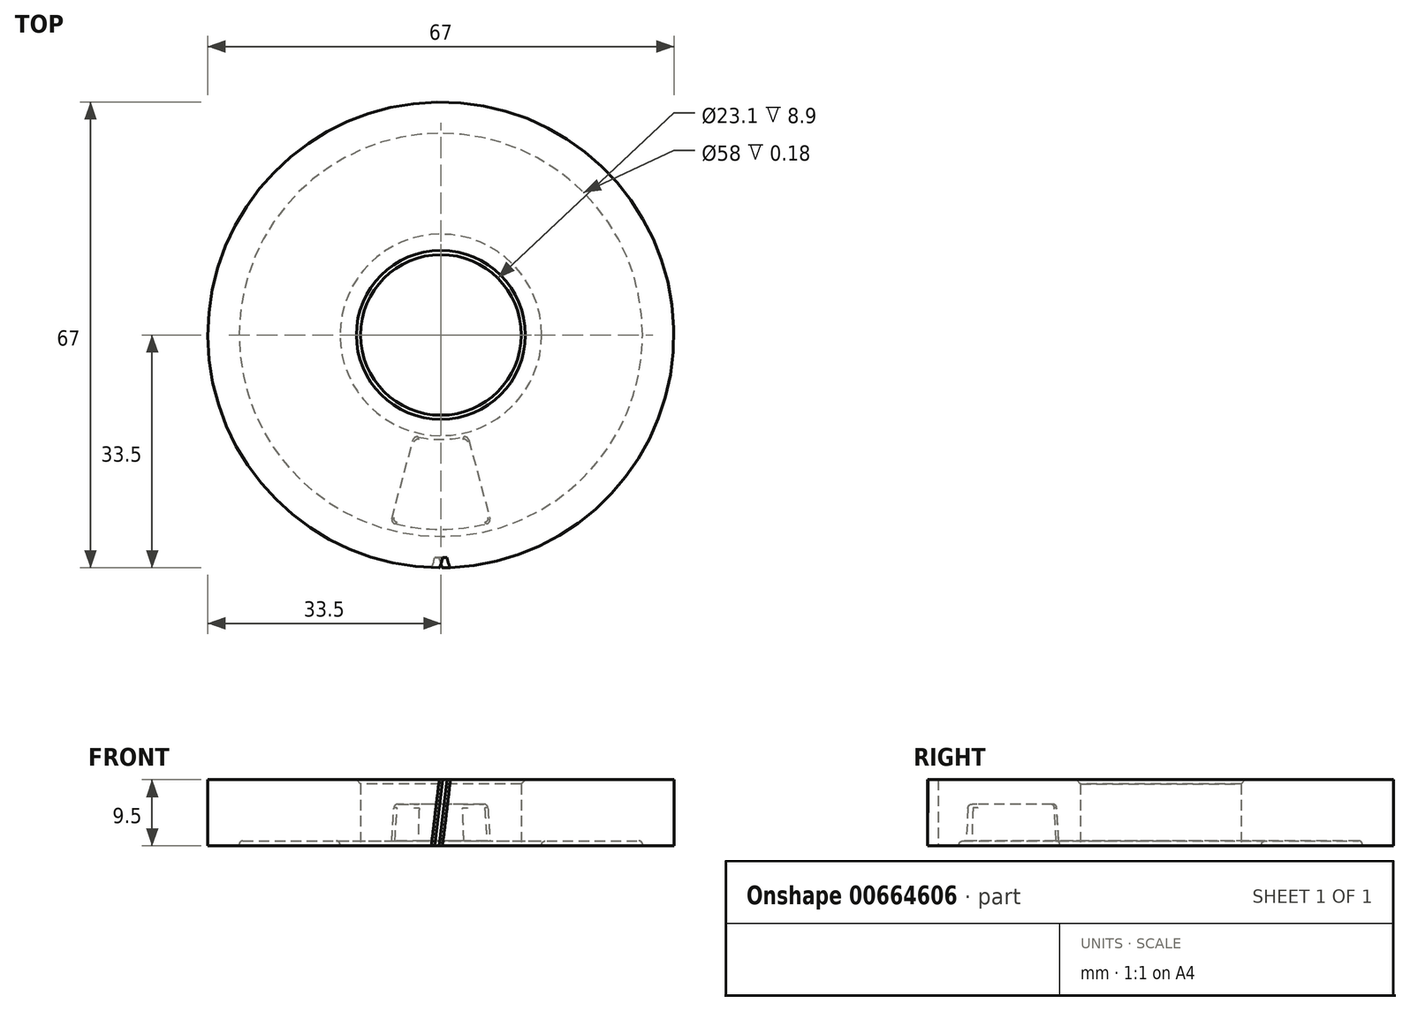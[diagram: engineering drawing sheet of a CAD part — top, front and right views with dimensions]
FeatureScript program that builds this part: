
annotation { "Feature Type Name" : "Feature", "Feature Type Description" : "" }
export const myFeature = defineFeature(function(context is Context, id is Id, definition is map)
    precondition{}
    {
        {
            var Q0;
            Q0=qCreatedBy(makeId("Top.planeOp"),FACE);
            var sketch = newSketch(context, id + "F0", { "sketchPlane" : qUnion([Q0])});
            skCircle(sketch, "E0", {"center": v(0, 0) * mm, "radius": 33.5 * mm});
            skCircle(sketch, "E1", {"center": v(0, 0) * mm, "radius": 11.55 * mm});
            skLineSegment(sketch, "E2", {"start": v(0, 55.87) * mm, "end": v(0, -59.32) * mm, "construction": true});
            skPoint(sketch, "E3", {"position": v(0, -33.5) * mm});
            skSolve(sketch);
        }
        {
            var Q0;
            Q0=makeQuery(id+"F0.imprint","IMPRINT",FACE,{"disambiguationData":[TD([[makeQuery(id+"F0.imprint","IMPRINT",EDGE,{"derivedFrom":sQuery(id+"F0.wireOp",EDGE,"E0")}),1.0]])]});
            extrude(context, id + "F1", {"entities" : qUnion([Q0]), "endBound" : BoundingType.SYMMETRIC, "depth" : 9.5 * mm, "offsetDistance" : 25 * mm});
        }
        {
            var Q0;
            Q0=makeQuery(id+"F1.opExtrude","CAP_EDGE",EDGE,{"disambiguationData":[OSD([sQuery(id+"F0.wireOp",EDGE,"E1")])],"isStart":false});
            chamfer(context, id + "F2", {"entities" : qUnion([Q0]), "width" : 0.6 * mm, "tangentPropagation" : true});
        }
        {
            var Q0;
            Q0=qCreatedBy(makeId("Front.planeOp"),FACE);
            var Q1;
            Q1=sQuery(id+"F0.wireOp",VERTEX,"E3");
            cPlane(context, id + "F3", {"entities" : qUnion([Q0, Q1]), "cplaneType" : CPlaneType.PLANE_POINT, "offset" : 25 * mm, "width" : 150 * mm, "height" : 150 * mm});
        }
        {
            var Q0;
            Q0=qCreatedBy(id+"F3.planeOp",FACE);
            var sketch = newSketch(context, id + "F4", { "sketchPlane" : qUnion([Q0])});
            skLineSegment(sketch, "E4", {"start": v(0, 7.46) * mm, "end": v(0, -4.64) * mm, "construction": true});
            skLineSegment(sketch, "E5", {"start": v(-0.11, 7.5) * mm, "end": v(1.9, 7.5) * mm, "construction": true});
            skLineSegment(sketch, "E6", {"start": v(1.9, 7.5) * mm, "end": v(0.11, -7.5) * mm, "construction": true});
            skLineSegment(sketch, "E7", {"start": v(0.11, -7.5) * mm, "end": v(-1.9, -7.5) * mm, "construction": true});
            skLineSegment(sketch, "E8", {"start": v(-1.9, -7.5) * mm, "end": v(-0.11, 7.5) * mm, "construction": true});
            skLineSegment(sketch, "E9", {"start": v(1.9, 7.5) * mm, "end": v(1.9, -9.24) * mm, "construction": true});
            skLineSegment(sketch, "E10", {"start": v(-1.9, -7.5) * mm, "end": v(-1.9, -9.39) * mm, "construction": true});
            skLineSegment(sketch, "E11", {"start": v(-12.57, 0) * mm, "end": v(13.12, 0) * mm, "construction": true});
            skSolve(sketch);
        }
        {
            var Q0;
            Q0=sQuery(id+"F4.wireOp",EDGE,"E6");
            var Q1;
            Q1=sQuery(id+"F0.wireOp",VERTEX,"E3");
            cPlane(context, id + "F5", {"entities" : qUnion([Q0, Q1]), "cplaneType" : CPlaneType.LINE_POINT, "offset" : 25 * mm, "width" : 150 * mm, "height" : 150 * mm});
        }
        {
            var Q0;
            Q0=qCreatedBy(id+"F5.planeOp",FACE);
            var sketch = newSketch(context, id + "F6", { "sketchPlane" : qUnion([Q0])});
            skEllipse(sketch, "E12", {"center": v(0, 0) * mm, "majorRadius": 33.66 * mm, "minorRadius": 33.5 * mm, "majorAxis": v(1, 0), "construction": true});
            skLineSegment(sketch, "E13", {"start": v(0, -5.25) * mm, "end": v(0, 45.83) * mm, "construction": true});
            skPoint(sketch, "E13.endSnap0", {"position": v(0, 33.5) * mm});
            skArc(sketch, "E14", {"start": v(-0.42, 32.5) * mm, "mid": v(-0.57, 33) * mm, "end": v(-0.8, 33.5) * mm});
            skLineSegment(sketch, "E15", {"start": v(0, 33.5) * mm, "end": v(4.9, 33.5) * mm, "construction": true});
            skLineSegment(sketch, "E16", {"start": v(0, 32) * mm, "end": v(-0.3, 32) * mm});
            skLineSegment(sketch, "E17", {"start": v(-0.3, 32) * mm, "end": v(-0.42, 32.5) * mm});
            skLineSegment(sketch, "E18.MirrorCS", {"start": v(0, 32) * mm, "end": v(0.3, 32) * mm});
            skLineSegment(sketch, "E19.MirrorCS", {"start": v(0.3, 32) * mm, "end": v(0.42, 32.5) * mm});
            skArc(sketch, "E20.MirrorCS", {"start": v(0.42, 32.5) * mm, "mid": v(0.57, 33) * mm, "end": v(0.8, 33.5) * mm});
            skArc(sketch, "E21", {"start": v(0.8, 33.5) * mm, "mid": v(0, 33.72) * mm, "end": v(-0.8, 33.5) * mm});
            skSolve(sketch);
        }
        {
            var Q0;
            Q0=makeQuery(id+"F6.imprint","IMPRINT",FACE,{"disambiguationData":[TD([[makeQuery(id+"F6.imprint","IMPRINT",EDGE,{"derivedFrom":sQuery(id+"F6.wireOp",EDGE,"E14")}),-1.0]])]});
            extrude(context, id + "F7", {"entities" : qUnion([Q0]), "operationType" : NewBodyOperationType.REMOVE, "endBound" : BoundingType.SYMMETRIC, "oppositeDirection" : true, "depth" : 25 * mm, "offsetDistance" : 25 * mm});
        }
        {
            var Q0;
            Q0=qCreatedBy(makeId("Front.planeOp"),FACE);
            var sketch = newSketch(context, id + "F8", { "sketchPlane" : qUnion([Q0])});
            skLineSegment(sketch, "E22", {"start": v(0, 91.64) * mm, "end": v(0, -90.78) * mm, "construction": true});
            skSolve(sketch);
        }
        {
            var Q0;
            Q0=makeQuery(id+"F1.opExtrude","CAP_FACE",FACE,{"disambiguationData":[OSD([sQuery(id+"F0.wireOp",EDGE,"E0"),sQuery(id+"F0.wireOp",EDGE,"E1")])],"isStart":true});
            var sketch = newSketch(context, id + "F9", { "sketchPlane" : qUnion([Q0])});
            skCircle(sketch, "E23", {"center": v(0, 0) * mm, "radius": 14.5 * mm});
            skCircle(sketch, "E24", {"center": v(0, 0) * mm, "radius": 29 * mm});
            skSolve(sketch);
        }
        {
            var Q0;
            Q0=makeQuery(id+"F9.imprint","IMPRINT",FACE,{"disambiguationData":[TD([[makeQuery(id+"F9.imprint","IMPRINT",EDGE,{"derivedFrom":sQuery(id+"F9.wireOp",EDGE,"E23")}),-1.0]])]});
            extrude(context, id + "F10", {"entities" : qUnion([Q0]), "operationType" : NewBodyOperationType.REMOVE, "oppositeDirection" : true, "depth" : 0.7 * mm, "offsetDistance" : 25 * mm});
        }
        {
            var Q0;
            Q0=makeQuery(id+"F1.opExtrude","CAP_FACE",FACE,{"disambiguationData":[OSD([sQuery(id+"F0.wireOp",EDGE,"E0"),sQuery(id+"F0.wireOp",EDGE,"E1")])],"isStart":true});
            var sketch = newSketch(context, id + "F11", { "sketchPlane" : qUnion([Q0])});
            skArc(sketch, "E25.0", {"start": v(-11.55, 0) * mm, "mid": v(9.16, -7.03) * mm, "end": v(-2.99, 11.16) * mm, "construction": true});
            skLineSegment(sketch, "E26", {"start": v(0, 43.8) * mm, "end": v(0, -44.82) * mm, "construction": true});
            skLineSegment(sketch, "E27", {"start": v(45.87, 0) * mm, "end": v(-44.82, 0) * mm, "construction": true});
            skArc(sketch, "E28", {"start": v(-28, 0) * mm, "mid": v(0, -28) * mm, "end": v(28, 0) * mm, "construction": true});
            skArc(sketch, "E29.0", {"start": v(-15, 0) * mm, "mid": v(-10.6, -10.6) * mm, "end": v(0, -15) * mm, "construction": true});
            skLineSegment(sketch, "E30", {"start": v(-2.99, 11.16) * mm, "end": v(-7.25, 27.05) * mm});
            skLineSegment(sketch, "E31", {"start": v(2.99, 11.16) * mm, "end": v(7.25, 27.05) * mm});
            skArc(sketch, "E32.trimOffspring", {"start": v(7.25, 27.05) * mm, "mid": v(0, 28) * mm, "end": v(-7.25, 27.05) * mm});
            skArc(sketch, "E33.trimOffspring", {"start": v(3.88, 14.49) * mm, "mid": v(0, 15) * mm, "end": v(-3.88, 14.49) * mm});
            skSolve(sketch);
        }
        {
            var Q0;
            {var subQ0=sQuery(id+"F11.wireOp",EDGE,"E32.trimOffspring");Q0=makeQuery(id+"F11.imprint","IMPRINT",FACE,{"disambiguationData":[TD([[makeQuery(id+"F11.imprint","IMPRINT",EDGE,{"derivedFrom":subQ0}),1.0]])]});}
            extrude(context, id + "F12", {"entities" : qUnion([Q0]), "operationType" : NewBodyOperationType.REMOVE, "oppositeDirection" : true, "depth" : 6 * mm, "offsetDistance" : 25 * mm, "hasDraft" : true, "draftAngle" : 3 * degree, "draftPullDirection" : true});
        }
        {
            var Q0;
            Q0=makeQuery(id+"F12.boolean.opBoolean","COPY",FACE,{"derivedFrom":makeQuery(id+"F12.opExtrude","CAP_FACE",FACE,{"disambiguationData":[OSD([sQuery(id+"F11.wireOp",EDGE,"E30"),sQuery(id+"F11.wireOp",EDGE,"E31"),sQuery(id+"F11.wireOp",EDGE,"E32.trimOffspring"),sQuery(id+"F11.wireOp",EDGE,"E33.trimOffspring")])],"isStart":false})});
            var Q1;
            Q1=makeQuery(id+"F12.boolean.opBoolean","COPY",EDGE,{"derivedFrom":makeQuery(id+"F12.opExtrude","SWEPT_EDGE",EDGE,{"disambiguationData":[OSD([sQuery(id+"F11.wireOp",EDGE,"E30"),sQuery(id+"F11.wireOp",EDGE,"E33.trimOffspring")])]})});
            var Q2;
            Q2=makeQuery(id+"F12.boolean.opBoolean","COPY",EDGE,{"derivedFrom":makeQuery(id+"F12.opExtrude","SWEPT_EDGE",EDGE,{"disambiguationData":[OSD([sQuery(id+"F11.wireOp",EDGE,"E31"),sQuery(id+"F11.wireOp",EDGE,"E33.trimOffspring")])]})});
            var Q3;
            Q3=makeQuery(id+"F12.boolean.opBoolean","COPY",EDGE,{"derivedFrom":makeQuery(id+"F12.opExtrude","SWEPT_EDGE",EDGE,{"disambiguationData":[OSD([sQuery(id+"F11.wireOp",EDGE,"E31"),sQuery(id+"F11.wireOp",EDGE,"E32.trimOffspring")])]})});
            var Q4;
            Q4=makeQuery(id+"F12.boolean.opBoolean","COPY",EDGE,{"derivedFrom":makeQuery(id+"F12.opExtrude","SWEPT_EDGE",EDGE,{"disambiguationData":[OSD([sQuery(id+"F11.wireOp",EDGE,"E30"),sQuery(id+"F11.wireOp",EDGE,"E32.trimOffspring")])]})});
            fillet(context, id + "F13", {"entities" : qUnion([Q0, Q1, Q2, Q3, Q4]), "radius" : 0.6 * mm, "tangentPropagation" : true, "allowEdgeOverflow" : false});
        }
        {
            var Q0;
            Q0=makeQuery(id+"F10.boolean.opBoolean","COPY",EDGE,{"derivedFrom":makeQuery(id+"F10.opExtrude","CAP_EDGE",EDGE,{"disambiguationData":[OSD([sQuery(id+"F9.wireOp",EDGE,"E24")])],"isStart":false})});
            var Q1;
            Q1=makeQuery(id+"F10.boolean.opBoolean","COPY",EDGE,{"derivedFrom":makeQuery(id+"F10.opExtrude","CAP_EDGE",EDGE,{"disambiguationData":[OSD([sQuery(id+"F9.wireOp",EDGE,"E23")])],"isStart":false})});
            fillet(context, id + "F14", {"entities" : qUnion([Q0, Q1]), "radius" : 0.52 * mm, "tangentPropagation" : true, "allowEdgeOverflow" : false});
        }
    });
